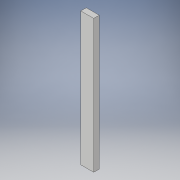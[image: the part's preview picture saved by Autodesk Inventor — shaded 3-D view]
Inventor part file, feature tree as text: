
AUTODESK INVENTOR PART (.ipt)
format: ipt  version: 2017 (Build 210142000, 142)  size: 92,160 bytes
history: native  units: in
note: dims shown in document units (in); Inventor stores cm internally (conversion verified against a paired STEP export)
features: extrude x1, sketch x1
ambient origin geometry x8: Origin, YZ Plane, XZ Plane, XY Plane, X Axis, Y Axis, Z Axis, Center Point
bodies: Solid1 (feature_tree)
feature tree (2):
  extrude  "Extrusion1"  Depth=1.5in
  sketch  "Sketch1"  dims[d0=3.5in d1=1.5in d2=36.0in d3=0.0in]
